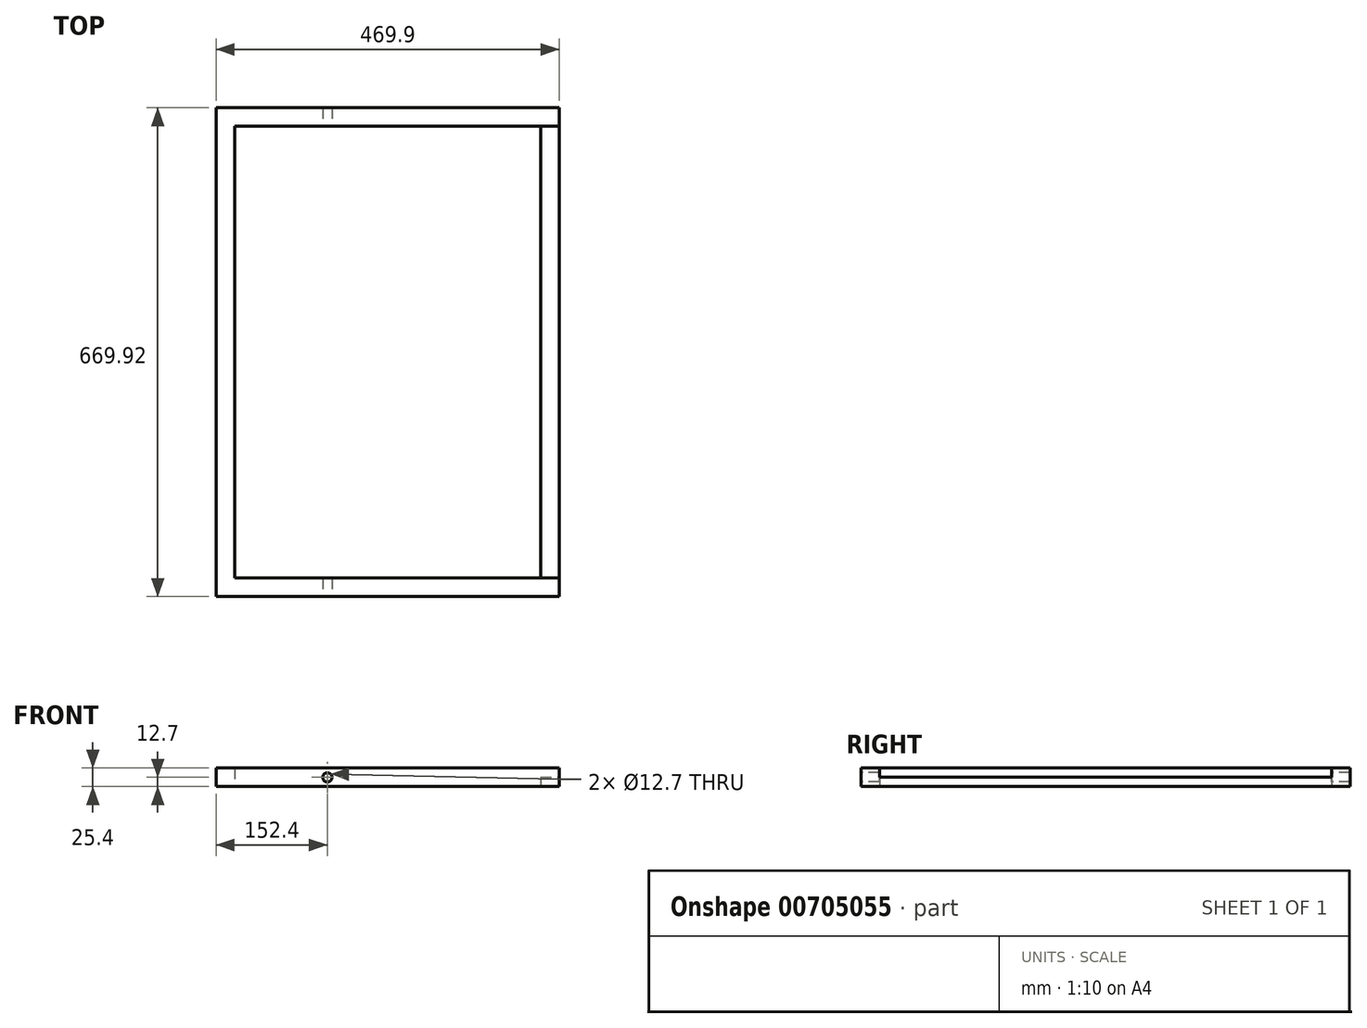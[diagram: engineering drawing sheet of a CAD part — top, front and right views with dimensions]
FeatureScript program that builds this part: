
annotation { "Feature Type Name" : "Feature", "Feature Type Description" : "" }
export const myFeature = defineFeature(function(context is Context, id is Id, definition is map)
    precondition{}
    {
        {
            var Q0;
            Q0=qCreatedBy(makeId("Top.planeOp"),FACE);
            var sketch = newSketch(context, id + "F0", { "sketchPlane" : qUnion([Q0])});
            skLineSegment(sketch, "E0.bottom", {"start": v(-234.95, 334.96) * mm, "end": v(234.95, 334.96) * mm});
            skLineSegment(sketch, "E0.top", {"start": v(-234.95, -334.96) * mm, "end": v(234.95, -334.96) * mm});
            skLineSegment(sketch, "E0.left", {"start": v(-234.95, 334.96) * mm, "end": v(-234.95, -334.96) * mm});
            skLineSegment(sketch, "E0.right", {"start": v(234.95, 334.96) * mm, "end": v(234.95, -334.96) * mm});
            skPoint(sketch, "E1", {"position": v(0, 334.96) * mm});
            skPoint(sketch, "E2", {"position": v(-234.95, 0) * mm});
            skLineSegment(sketch, "E3.bottom", {"start": v(-209.55, 309.56) * mm, "end": v(209.55, 309.56) * mm});
            skLineSegment(sketch, "E3.top", {"start": v(-209.55, -309.56) * mm, "end": v(209.55, -309.56) * mm});
            skLineSegment(sketch, "E3.left", {"start": v(-209.55, 309.56) * mm, "end": v(-209.55, -309.56) * mm});
            skLineSegment(sketch, "E3.right", {"start": v(209.55, 309.56) * mm, "end": v(209.55, -309.56) * mm});
            skLineSegment(sketch, "E4", {"start": v(209.55, 309.56) * mm, "end": v(234.95, 309.56) * mm});
            skLineSegment(sketch, "E5", {"start": v(209.55, -309.56) * mm, "end": v(234.95, -309.56) * mm});
            skSolve(sketch);
        }
        {
            var Q0;
            {var subQ1=sQuery(id+"F0.wireOp",EDGE,"E0.bottom");Q0=makeQuery(id+"F0.imprint","IMPRINT",FACE,{"disambiguationData":[TD([[makeQuery(id+"F0.imprint","IMPRINT",EDGE,{"derivedFrom":subQ1}),-1.0]])]});}
            extrude(context, id + "F1", {"entities" : qUnion([Q0]), "depth" : 25.4 * mm, "offsetDistance" : 25.4 * mm});
        }
        {
            var Q0;
            Q0=makeQuery(id+"F0.imprint","IMPRINT",FACE,{"disambiguationData":[TD([[makeQuery(id+"F0.imprint","IMPRINT",EDGE,{"derivedFrom":sQuery(id+"F0.wireOp",EDGE,"E3.right")}),1.0]])]});
            extrude(context, id + "F2", {"entities" : qUnion([Q0]), "operationType" : NewBodyOperationType.ADD, "depth" : 12.7 * mm, "offsetDistance" : 25.4 * mm});
        }
        {
            var Q0;
            Q0=makeQuery(id+"F1.opExtrude","SWEPT_FACE",FACE,{"disambiguationData":[OSD([sQuery(id+"F0.wireOp",EDGE,"E0.top")])]});
            var sketch = newSketch(context, id + "F3", { "sketchPlane" : qUnion([Q0])});
            skPoint(sketch, "E6", {"position": v(-234.95, 12.7) * mm});
            skPoint(sketch, "E7", {"position": v(-82.55, 12.7) * mm});
            skCircle(sketch, "E8", {"center": v(-82.55, 12.7) * mm, "radius": 6.35 * mm});
            skSolve(sketch);
        }
        {
            var Q0;
            Q0 = qSketchRegion(id + "F3", true);
            extrude(context, id + "F4", {"entities" : qUnion([Q0]), "operationType" : NewBodyOperationType.REMOVE, "oppositeDirection" : true, "depth" : 762 * mm, "offsetDistance" : 25.4 * mm});
        }
    });
